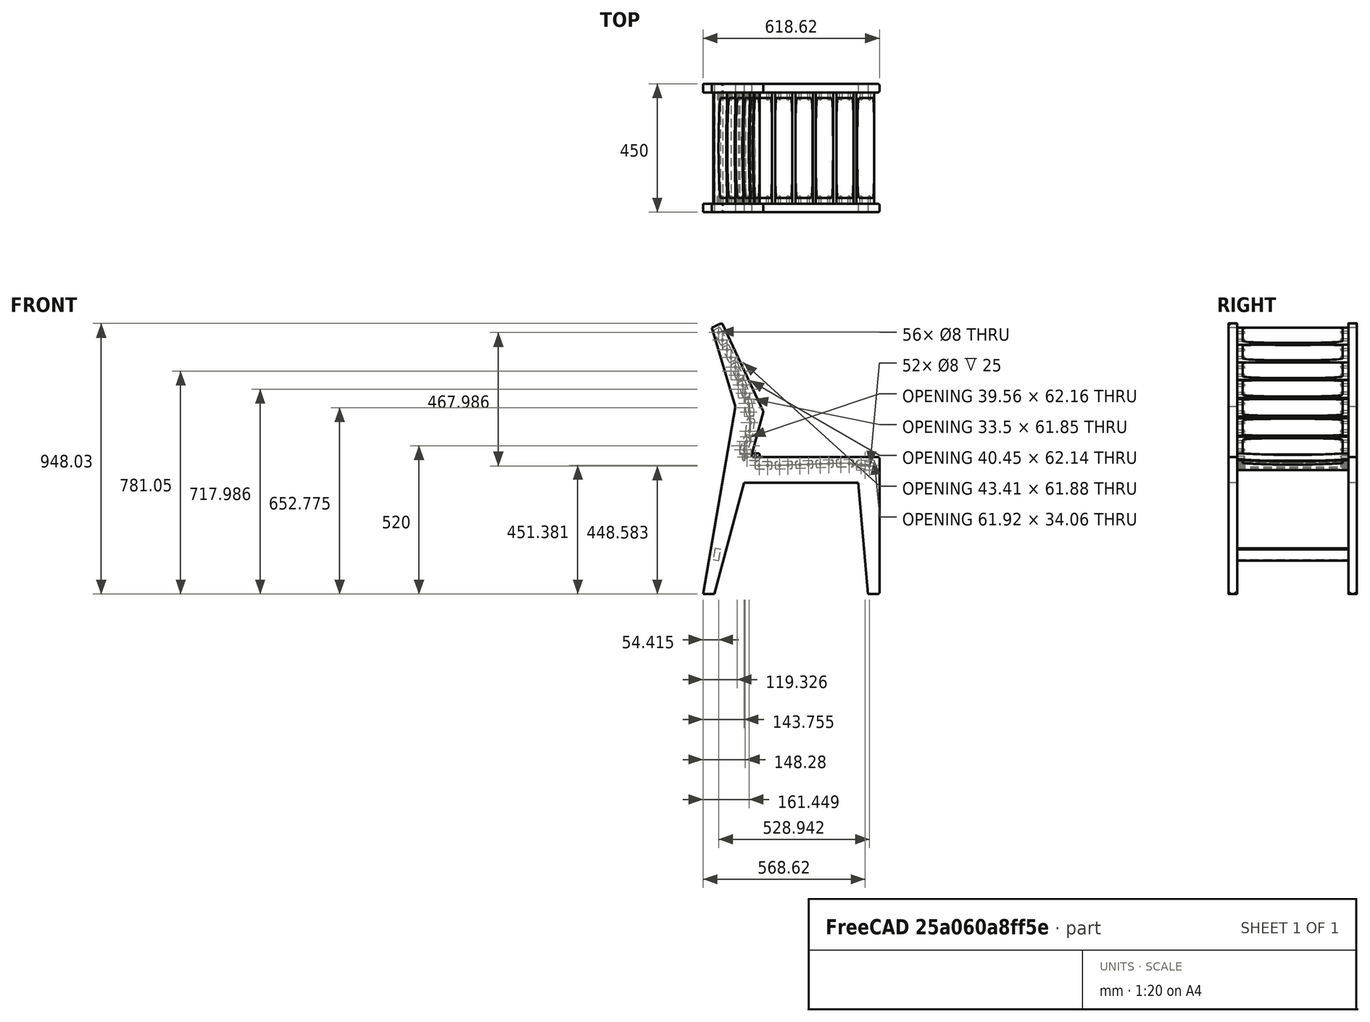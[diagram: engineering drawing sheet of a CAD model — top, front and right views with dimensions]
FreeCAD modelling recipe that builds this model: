
FCSTD DOCUMENT  (FreeCAD 0.21R33771 (Git))
Label: office_v2
License: All rights reserved
LicenseURL: http://en.wikipedia.org/wiki/All_rights_reserved
objects: TechDraw::DrawViewDimension×39, Sketcher::SketchObject×8, PartDesign::Body×4, TechDraw::DrawProjGroupItem×4, PartDesign::Pad×3, Part::FeaturePython×3, TechDraw::DrawSVGTemplate×3, TechDraw::DrawPage×3, PartDesign::Hole×2, PartDesign::SubShapeBinder×2, TechDraw::DrawProjGroup×2, TechDraw::DrawViewBalloon×2, Spreadsheet::Sheet×1, PartDesign::Fillet×1, PartDesign::Pocket×1, TechDraw::DrawViewPart×1, App::Part×1, PartDesign::Boolean×1
note: 92 computed .brp shape members not serialized (recipe doc carries the construction recipe); baked Part::Feature solids carry a one-line shape summary decoded from their .brp

FEATURE [Sketcher::SketchObject] Sketch  label="SideSketch"
  FullyConstrained = true
  Placement = pos=(0,0,0) rot=(1,0,0;1.5708rad)
  expr: Constraints[23] = <<Spreadsheet>>.back_angle
  expr: Constraints[24] = <<Spreadsheet>>.back_leg_angle
  expr: Constraints[29] = <<Spreadsheet>>.seat_length
  expr: Constraints[30] = <<Spreadsheet>>.lumbar_end_height
  expr: Constraints[32] = <<Spreadsheet>>.total_height
  expr: Constraints[5] = <<Spreadsheet>>.seat_height
  sketch-geometry (28):
    g0: LineSegment StartX=0 StartY=0 StartZ=0 EndX=450 EndY=0 EndZ=0
    g1: LineSegment StartX=375.879 StartY=-90 StartZ=0 EndX=-24.1154 EndY=-90 EndZ=0
    g2: LineSegment StartX=450 StartY=0 StartZ=0 EndX=450 EndY=-480 EndZ=0
    g3: LineSegment StartX=450 StartY=-480 StartZ=0 EndX=410 EndY=-480 EndZ=0
    g4: LineSegment StartX=410 StartY=-480 StartZ=0 EndX=368.005 EndY=0 EndZ=0
    g5: LineSegment StartX=-168.616 StartY=-480 StartZ=0 EndX=-128.616 EndY=-480 EndZ=0
    g6: LineSegment StartX=-101.684 StartY=470 StartZ=0 EndX=-137.936 EndY=453.095 EndZ=0
    g7: LineSegment StartX=-137.936 StartY=453.095 StartZ=0 EndX=-55.6825 EndY=176.942 EndZ=0
    g8: LineSegment StartX=-168.616 StartY=-480 StartZ=0 EndX=-55.6825 EndY=176.942 EndZ=0
    g9: LineSegment StartX=-55.6825 StartY=176.942 StartZ=0 EndX=42.8719 EndY=160 EndZ=0
    g10: LineSegment StartX=-128.616 StartY=-480 StartZ=0 EndX=42.8719 EndY=160 EndZ=0
    g11: LineSegment StartX=-101.684 StartY=470 StartZ=0 EndX=42.8719 EndY=160 EndZ=0
    g12: LineSegment StartX=-137.936 StartY=453.095 StartZ=0 EndX=-101.684 EndY=470 EndZ=0
    g13: LineSegment StartX=-101.684 StartY=470 StartZ=0 EndX=42.8719 EndY=160 EndZ=0
    g14: LineSegment StartX=42.8719 StartY=160 StartZ=0 EndX=0 EndY=0 EndZ=0
    g15: LineSegment StartX=0 StartY=0 StartZ=0 EndX=450 EndY=0 EndZ=0
    g16: LineSegment StartX=450 StartY=0 StartZ=0 EndX=450 EndY=-480 EndZ=0
    g17: LineSegment StartX=450 StartY=-480 StartZ=0 EndX=410 EndY=-480 EndZ=0
    g18: LineSegment StartX=410 StartY=-480 StartZ=0 EndX=375.879 EndY=-90 EndZ=0
    g19: LineSegment StartX=375.879 StartY=-90 StartZ=0 EndX=-24.1154 EndY=-90 EndZ=0
    g20: LineSegment StartX=-24.1154 StartY=-90 StartZ=0 EndX=-128.616 EndY=-480 EndZ=0
    g21: LineSegment StartX=-128.616 StartY=-480 StartZ=0 EndX=-168.616 EndY=-480 EndZ=0
    g22: LineSegment StartX=-168.616 StartY=-480 StartZ=0 EndX=-55.6825 EndY=176.942 EndZ=0
    g23: LineSegment StartX=-55.6825 StartY=176.942 StartZ=0 EndX=-137.936 EndY=453.095 EndZ=0
    g24: LineSegment StartX=-125.99 StartY=-320.578 StartZ=0 EndX=-106.279 EndY=-323.967 EndZ=0
    g25: LineSegment StartX=-106.279 StartY=-323.967 StartZ=0 EndX=-113.056 EndY=-363.388 EndZ=0
    g26: LineSegment StartX=-113.056 StartY=-363.388 StartZ=0 EndX=-132.767 EndY=-360 EndZ=0
    g27: LineSegment StartX=-132.767 StartY=-360 StartZ=0 EndX=-125.99 EndY=-320.578 EndZ=0
  constraints (75):
    c: Horizontal(g0)
    c: Horizontal(g1)
    c: Coincident(g2,g3)
    c: Horizontal(g3)
    c: Coincident(g4,g3)
    c: DistanceY(g2,g0) = 480
    c: PointOnObject(g5,g3)
    c: Coincident(g2,g0)
    c: Perpendicular(g2,g0)
    c: DistanceX(g3,g2) = 40
    c: Angle(g1,g4) = 1.65806
    c: Horizontal(g5)
    c: DistanceY(g1,g0) = 90
    c: Coincident(g7,g6)
    c: Coincident(g8,g5)
    c: DistanceX(g5,g5) = 40
    c: Coincident(g7,g8)
    c: Coincident(g9,g7)
    c: Angle(g8,g9) = 1.5708
    c: Coincident(g10,g5)
    c: Coincident(g11,g6)
    c: Coincident(g11,g10)
    c: Coincident(g10,g9)
    c: Angle(g0,g11) = 2.00713
    c: Angle(g10,g1) = 1.8326
    c: PointOnObject(g0,g10)
    c: PointOnObject(g1,g10)
    c: Perpendicular(g11,g6)
    c: Coincident(g0,g-1)
    c: Distance(g0) = 450
    c: Distance(g9,g0) = 160
    c: Distance(g9) = 100
    c: DistanceY(g5,g6) = 950
    c: Equal(g6,g5)
    c: PointOnObject(g4,g0)
    c: PointOnObject(g1,g4)
    c: Coincident(g6,g12)
    c: Coincident(g12,g6)
    c: Coincident(g12,g13)
    c: Coincident(g13,g9)
    c: Coincident(g13,g14)
    c: Coincident(g14,g0)
    c: Coincident(g14,g15)
    c: Coincident(g15,g0)
    c: Coincident(g15,g16)
    c: Coincident(g16,g2)
    c: Coincident(g16,g17)
    c: Coincident(g17,g3)
    c: Coincident(g17,g18)
    c: Coincident(g18,g1)
    c: Coincident(g18,g19)
    c: Coincident(g19,g1)
    c: Coincident(g19,g20)
    c: Coincident(g20,g5)
    c: Coincident(g20,g21)
    c: Coincident(g21,g5)
    c: Coincident(g21,g22)
    c: Coincident(g22,g7)
    c: Coincident(g22,g23)
    c: Coincident(g23,g12)
    c: Coincident(g24,g25)
    c: Coincident(g25,g26)
    c: Coincident(g26,g27)
    c: Coincident(g27,g24)
    c: Perpendicular(g25,g24)
    c: Perpendicular(g26,g25)
    c: Perpendicular(g26,g27)
    c: Parallel(g27,g22)
    c: Distance(g24,g22) = 15
    c: Distance(g25) = 40
    c: DistanceY(g20,g26) = 120
    c: Distance(g26) = 20
    c: Angle(g12,g13) = 1.5708
    c: Angle(g13,g9) = 0.964221
    c: Angle(g9,g23) = 2.03053
FEATURE [Spreadsheet::Sheet] Spreadsheet
  cells = A1='seat length; B1(seat_length)=450; A2='seat height; B2(seat_height)=480; A3='back angle; B3(back_angle)=115; A4='chair width; B4(chair_width)=450; A5='slats thickness; B5(slat_thickness)=25; A6='back slats height; B6(back_slat_width)=60; A7='seat slats width; B7(seat_slat_width)=80; A8='seat slats thickness; B8(seat_slat_thickness)=20; A9='total height; B9(total_height)=950; A10='lumbar support end height; B10(lumbar_end_height)=160; A11='back slat gap; B11(back_slat_gap)=15; A12='back slat thickness; B12(back_slat_thickness)=20; A13='seat slat gap; B13(seat_slat_gap)=10; A14='back leg angle to surface; B14(back_leg_angle)=105; A15='draft back; B15(draft_back)=5; A16='side thickness; B16(side_thickness)=30; A17='slat_width; B17(slat_width)=60; A18='slat_chamfer_radius; B18(slat_chamfer_radius)=5
FEATURE [PartDesign::Pad] Pad
  Direction = (0,-1,2e-16)
  Length = 30
  Length2 = 10
  Placement = pos=(0,0,0) rot=(1,0,0;1.5708rad)
  Profile = -> Sketch
  ReferenceAxis = -> Sketch [N_Axis]
  Type = 0
  expr: Length = <<Spreadsheet>>.side_thickness
FEATURE [PartDesign::Fillet] Fillet
  Base = -> Pad [Face2,Face3,Face4,Face5]
  BaseFeature = -> Pad
  Placement = pos=(0,0,0) rot=(1,0,0;1.5708rad)
  Radius = 6
  SupportTransform = false
  UseAllEdges = false
FEATURE [PartDesign::Body] Body  label="LeftSide"
  Group = -> [Sketch,Pad,Fillet]
  Origin = -> Origin
  Tip = -> Fillet
FEATURE [Sketcher::SketchObject] Sketch001  label="curves"
  ExternalGeometry = -> [Sketch]
  FullyConstrained = false
  MapMode = 5
  Placement = pos=(0,-1.72e-14,0) rot=(-1,0,0;1.5708rad)
  Support = -> [Pad]
  sketch-geometry (23):
    g0: LineSegment StartX=375.879 StartY=90 StartZ=0 EndX=368.005 EndY=0 EndZ=0
    g1: LineSegment StartX=0 StartY=0 StartZ=0 EndX=-24.1154 EndY=90 EndZ=0
    g2: LineSegment StartX=42.8719 StartY=-160 StartZ=0 EndX=-55.6825 EndY=-176.942 EndZ=0
    g3: Circle CenterX=-107.436 CenterY=-423.182 CenterZ=0 NormalX=0 NormalY=0 NormalZ=1 AngleXU=0 Radius=1
    g4: Circle CenterX=4.19663 CenterY=-116.283 CenterZ=0 NormalX=0 NormalY=0 NormalZ=1 AngleXU=0 Radius=1
    g5: Circle CenterX=-20.3403 CenterY=-40 CenterZ=0 NormalX=0 NormalY=0 NormalZ=1 AngleXU=0 Radius=1
    g6: BSplineCurve PolesCount=6 KnotsCount=4 Degree=3 IsPeriodic=0
    g7: GeomPoint X=-107.436 Y=-423.182 Z=0
    g8: GeomPoint X=-6.41239 Y=-168.472 Z=0
    g9: GeomPoint X=-20.3403 Y=-40 Z=0
    g10: Circle CenterX=-67.1086 CenterY=-343.425 CenterZ=0 NormalX=0 NormalY=0 NormalZ=1 AngleXU=0 Radius=0.962105
    g11: Circle CenterX=-16.1135 CenterY=-229.617 CenterZ=0 NormalX=0 NormalY=0 NormalZ=1 AngleXU=0 Radius=0.629843
    g12: Circle CenterX=-5.01988 CenterY=-156.601 CenterZ=0 NormalX=0 NormalY=0 NormalZ=1 AngleXU=0 Radius=1
    g13: GeomPoint X=-31.7882 Y=-257.283 Z=0
    g14: Circle CenterX=400 CenterY=28.6187 CenterZ=0 NormalX=0 NormalY=0 NormalZ=1 AngleXU=0 Radius=1
    g15: Circle CenterX=43.0206 CenterY=29.1813 CenterZ=0 NormalX=0 NormalY=0 NormalZ=1 AngleXU=0 Radius=1
    g16: BSplineCurve PolesCount=5 KnotsCount=3 Degree=3 IsPeriodic=0
    g17: GeomPoint X=400 Y=28.6187 Z=0
    g18: GeomPoint X=43.0206 Y=29.1813 Z=0
    g19: Circle CenterX=358.23 CenterY=20.6863 CenterZ=0 NormalX=0 NormalY=0 NormalZ=1 AngleXU=0 Radius=1
    g20: Circle CenterX=277.297 CenterY=21.6556 CenterZ=0 NormalX=0 NormalY=0 NormalZ=1 AngleXU=0 Radius=1
    g21: Circle CenterX=111.923 CenterY=30.2855 CenterZ=0 NormalX=0 NormalY=0 NormalZ=1 AngleXU=0 Radius=1
    g22: GeomPoint X=274.038 Y=22.8992 Z=0
  constraints (40):
    c: Coincident(g0,g-6)
    c: Parallel(g0,g-5)
    c: Coincident(g1,g-14)
    c: Coincident(g1,g-7)
    c: PointOnObject(g0,g-14)
    c: Coincident(g2,g-13)
    c: Coincident(g2,g-10)
    c: Weight(g3) = 1
    c: Equal(g3,g4)
    c: Equal(g3,g5)
    c: InternalAlignment(g3,g6)
    c: InternalAlignment(g4,g6)
    c: InternalAlignment(g5,g6)
    c: InternalAlignment(g7,g6)
    c: InternalAlignment(g8,g6)
    c: InternalAlignment(g9,g6)
    c: Distance(g6,g-11) = 40
    c: DistanceY(g-1,g6) = -40
    c: InternalAlignment(g10,g6)
    c: InternalAlignment(g11,g6)
    c: InternalAlignment(g12,g6)
    c: Equal(g12,g3)
    c: InternalAlignment(g13,g6)
    c: Distance(g6,g-12) = 25
    c: Distance(g6,g-13) = 30
    c: PointOnObject(g8,g2)
    c: Weight(g14) = 1
    c: Equal(g14,g15)
    c: InternalAlignment(g14,g16)
    c: InternalAlignment(g15,g16)
    c: InternalAlignment(g17,g16)
    c: InternalAlignment(g18,g16)
    c: Distance(g16,g-3) = 50
    c: InternalAlignment(g19,g16)
    c: Equal(g19,g14)
    c: InternalAlignment(g20,g16)
    c: Equal(g20,g14)
    c: InternalAlignment(g21,g16)
    c: Equal(g21,g14)
    c: InternalAlignment(g22,g16)
FEATURE [Sketcher::SketchObject] Sketch002  label="slat_profile"
  FullyConstrained = true
  MapMode = 5
  Placement = pos=(0,0,0) rot=(1,0,0;1.5708rad)
  Support = -> [XZ_Plane001]
  expr: Constraints[15] = <<Spreadsheet>>.slat_width
  expr: Constraints[16] = <<Spreadsheet>>.slat_thickness
  expr: Constraints[17] = <<Spreadsheet>>.slat_chamfer_radius
  sketch-geometry (9):
    g0: ArcOfCircle CenterX=25 CenterY=-7.5 CenterZ=0 NormalX=0 NormalY=0 NormalZ=1 AngleXU=0 Radius=5 StartAngle=4.71239 EndAngle=6.28319
    g1: LineSegment StartX=25 StartY=-12.5 StartZ=0 EndX=-25 EndY=-12.5 EndZ=0
    g2: ArcOfCircle CenterX=-25 CenterY=-7.5 CenterZ=0 NormalX=0 NormalY=0 NormalZ=1 AngleXU=0 Radius=5 StartAngle=3.14159 EndAngle=4.71239
    g3: LineSegment StartX=-30 StartY=-7.5 StartZ=0 EndX=-30 EndY=7.5 EndZ=0
    g4: ArcOfCircle CenterX=-25 CenterY=7.5 CenterZ=0 NormalX=0 NormalY=0 NormalZ=1 AngleXU=0 Radius=5 StartAngle=1.5708 EndAngle=3.14159
    g5: LineSegment StartX=-25 StartY=12.5 StartZ=0 EndX=25 EndY=12.5 EndZ=0
    g6: ArcOfCircle CenterX=25 CenterY=7.5 CenterZ=0 NormalX=0 NormalY=0 NormalZ=1 AngleXU=0 Radius=5 StartAngle=1e-16 EndAngle=1.5708
    g7: LineSegment StartX=30 StartY=7.5 StartZ=0 EndX=30 EndY=-7.5 EndZ=0
    g8: GeomPoint X=-30 Y=12.5 Z=0
  constraints (20):
    c: Tangent(g0,g1) = 1.5708
    c: Tangent(g1,g2) = 1.5708
    c: Tangent(g2,g3) = 1.5708
    c: Tangent(g3,g4) = 1.5708
    c: Tangent(g4,g5) = 1.5708
    c: Tangent(g5,g6) = 1.5708
    c: Tangent(g6,g7) = 1.5708
    c: Tangent(g7,g0) = 1.5708
    c: Equal(g0,g2)
    c: Equal(g2,g4)
    c: Equal(g4,g6)
    c: PointOnObject(g8,g3)
    c: PointOnObject(g8,g5)
    c: Parallel(g5,g1)
    c: Perpendicular(g1,g7)
    c: Distance(g6,g3) = 60
    c: Distance(g1,g4) = 25
    c: Distance(g2,g2) = 5
    c: Symmetric(g3,g6,g-2)
    c: Symmetric(g5,g0,g-1)
FEATURE [PartDesign::Pad] Pad001
  Direction = (0,-1,2e-16)
  Length = 390
  Length2 = 10
  Placement = pos=(0,0,0) rot=(1,0,0;1.5708rad)
  Profile = -> Sketch002
  ReferenceAxis = -> Sketch002 [N_Axis]
  Reversed = true
  Type = 0
  expr: Length = <<Spreadsheet>>.chair_width - <<Spreadsheet>>.side_thickness * 2
FEATURE [Sketcher::SketchObject] Sketch003
  ExternalGeometry = -> [Pad001]
  FullyConstrained = true
  MapMode = 5
  Placement = pos=(0,0,0) rot=(1,0,0;1.5708rad)
  Support = -> [Pad001]
  expr: Constraints[0] = <<Spreadsheet>>.slat_thickness / 2
  sketch-geometry (2):
    g0: Circle CenterX=15 CenterY=-7.1e-15 CenterZ=0 NormalX=0 NormalY=0 NormalZ=1 AngleXU=0 Radius=4
    g1: Circle CenterX=-15 CenterY=0 CenterZ=0 NormalX=0 NormalY=0 NormalZ=1 AngleXU=0 Radius=4
  constraints (7):
    c: Distance(g0,g-3) = 12.5
    c: Distance(g0,g-4) = 15
    c: Diameter(g0) = 8
    c: Diameter(g1) = 8
    c: PointOnObject(g1,g-1)
    c: Distance(g1,g-5) = 15
    c: Distance(g1,g0) = 30
FEATURE [PartDesign::Hole] Hole
  BaseFeature = -> Pad001
  CustomThreadClearance = 0
  Depth = 25
  DepthType = 0
  Diameter = 8
  DrillForDepth = false
  DrillPoint = 1
  DrillPointAngle = 118
  HoleCutCountersinkAngle = 90
  HoleCutCustomValues = false
  HoleCutDepth = 0
  HoleCutDiameter = 6.1
  HoleCutType = 0
  ModelThread = false
  Placement = pos=(0,0,0) rot=(1,0,0;1.5708rad)
  Profile = -> Sketch003
  Tapered = false
  TaperedAngle = 90
  ThreadClass = 0
  ThreadDepth = 25
  ThreadDepthType = 0
  ThreadDirection = 0
  ThreadFit = 0
  ThreadSize = 0
  ThreadType = 0
  Threaded = false
  UseCustomThreadClearance = false
FEATURE [PartDesign::SubShapeBinder] Binder
  BindCopyOnChange = 0
  BindMode = 0
  ClaimChildren = false
  Context = -> Body001 [Binder.]
  Fuse = false
  MakeFace = true
  OffsetFill = false
  OffsetIntersection = false
  OffsetJoinType = 0
  OffsetOpenResult = false
  PartialLoad = false
  Relative = true
  Support = -> [Body]
  _Version = 2
FEATURE [Sketcher::SketchObject] Sketch004
  ExternalGeometry = -> [Hole]
  FullyConstrained = true
  MapMode = 5
  Placement = pos=(0,390,0) rot=(-1,0,0;1.5708rad)
  Support = -> [Hole]
  sketch-geometry (2):
    g0: Circle CenterX=-15 CenterY=0 CenterZ=0 NormalX=0 NormalY=0 NormalZ=1 AngleXU=0 Radius=4
    g1: Circle CenterX=15 CenterY=0 CenterZ=0 NormalX=0 NormalY=0 NormalZ=1 AngleXU=0 Radius=4
  constraints (6):
    c: PointOnObject(g0,g-1)
    c: PointOnObject(g1,g-1)
    c: Diameter(g0) = 8
    c: Diameter(g1) = 8
    c: Distance(g1,g-4) = 15
    c: Distance(g0,g-6) = 15
FEATURE [PartDesign::Hole] Hole001
  BaseFeature = -> Hole
  CustomThreadClearance = 0
  Depth = 25
  DepthType = 0
  Diameter = 8
  DrillForDepth = false
  DrillPoint = 1
  DrillPointAngle = 118
  HoleCutCountersinkAngle = 90
  HoleCutCustomValues = false
  HoleCutDepth = 0
  HoleCutDiameter = 6.1
  HoleCutType = 0
  ModelThread = false
  Placement = pos=(0,0,0) rot=(1,0,0;1.5708rad)
  Profile = -> Sketch004
  Tapered = false
  TaperedAngle = 90
  ThreadClass = 0
  ThreadDepth = 25
  ThreadDepthType = 0
  ThreadDirection = 0
  ThreadFit = 0
  ThreadSize = 0
  ThreadType = 0
  Threaded = false
  UseCustomThreadClearance = false
FEATURE [Part::FeaturePython] Clone  label="RightSide"  # Draft clone (typed FeaturePython)
  AttacherType = Attacher::AttachEngine3D
  Fuse = false
  Objects = -> [Body]
  Placement = pos=(0,420,0) rot=(0,0,1;0rad)
  Scale = (1,1,1)
  expr: .Placement.Base.y = <<Spreadsheet>>.chair_width - <<Spreadsheet>>.side_thickness
FEATURE [Sketcher::SketchObject] Sketch005
  ExternalGeometry = -> [Hole001]
  FullyConstrained = true
  MapMode = 5
  Placement = pos=(30,0,0) rot=(0.707107,0,0.707107;3.14159rad)
  Support = -> [Hole001]
  sketch-geometry (4):
    g0: GeomPoint X=12.5 Y=-20 Z=0
    g1: GeomPoint X=12.5 Y=-370 Z=0
    g2: ArcOfCircle CenterX=3072.5 CenterY=-195 CenterZ=0 NormalX=0 NormalY=0 NormalZ=1 AngleXU=0 Radius=3065 StartAngle=3.08447 EndAngle=3.19872
    g3: LineSegment StartX=12.5 StartY=-20 StartZ=0 EndX=12.5 EndY=-370 EndZ=0
  constraints (9):
    c: PointOnObject(g0,g-3)
    c: PointOnObject(g1,g-3)
    c: Distance(g0,g-3) = 20
    c: Distance(g1,g-3) = 20
    c: Coincident(g2,g0)
    c: Coincident(g2,g1)
    c: Tangent(g2,g-4)
    c: Coincident(g3,g2)
    c: Coincident(g3,g2)
FEATURE [PartDesign::Pocket] Pocket
  BaseFeature = -> Hole001
  Direction = (-1,0,2e-16)
  Length = 64
  Length2 = 5
  Placement = pos=(0,0,0) rot=(1,0,0;1.5708rad)
  Profile = -> Sketch005
  ReferenceAxis = -> Sketch005 [N_Axis]
  Type = 4
FEATURE [PartDesign::Body] Body001  label="Slat"
  Group = -> [Sketch002,Pad001,Sketch003,Hole,Binder,Sketch001,Sketch004,Hole001,Sketch005,Pocket]
  Origin = -> Origin001
  Tip = -> Pocket
FEATURE [PartDesign::SubShapeBinder] Binder001
  BindCopyOnChange = 0
  BindMode = 0
  ClaimChildren = false
  Context = -> Body002 [Binder001.]
  Fuse = false
  MakeFace = true
  OffsetFill = false
  OffsetIntersection = false
  OffsetJoinType = 0
  OffsetOpenResult = false
  PartialLoad = false
  Relative = true
  Support = -> [Body[Fillet.Face2]]
  _Version = 2
FEATURE [Sketcher::SketchObject] Sketch006
  ExternalGeometry = -> [Binder001]
  FullyConstrained = true
  MapMode = 5
  Placement = pos=(0,0,0) rot=(1,0,0;1.5708rad)
  Support = -> [XZ_Plane002]
  sketch-geometry (4):
    g0: LineSegment StartX=-106.279 StartY=-323.967 StartZ=0 EndX=-125.99 EndY=-320.578 EndZ=0
    g1: LineSegment StartX=-125.99 StartY=-320.578 StartZ=0 EndX=-132.767 EndY=-360 EndZ=0
    g2: LineSegment StartX=-132.767 StartY=-360 StartZ=0 EndX=-113.056 EndY=-363.388 EndZ=0
    g3: LineSegment StartX=-113.056 StartY=-363.388 StartZ=0 EndX=-106.279 EndY=-323.967 EndZ=0
  constraints (12):
    c: Coincident(g0,g1)
    c: Coincident(g1,g2)
    c: Coincident(g2,g3)
    c: Coincident(g3,g0)
    c: Distance(g1) = 40
    c: Distance(g0) = 20
    c: Parallel(g0,g2)
    c: Parallel(g3,g1)
    c: Parallel(g1,g-3)
    c: Perpendicular(g2,g3)
    c: DistanceY(g-5,g1) = 120
    c: Distance(g1,g-3) = 15
FEATURE [PartDesign::Pad] Pad002
  Direction = (0,-1,-2e-16)
  Length = 390
  Length2 = 10
  Placement = pos=(0,0,0) rot=(1,0,0;1.5708rad)
  Profile = -> Sketch006
  ReferenceAxis = -> Sketch006 [N_Axis]
  Reversed = true
  Type = 0
  expr: Length = <<Spreadsheet>>.chair_width - 2 * <<Spreadsheet>>.side_thickness
FEATURE [PartDesign::Body] Body002  label="Stretcher"
  Group = -> [Binder001,Sketch006,Pad002]
  Origin = -> Origin002
  Tip = -> Pad002
FEATURE [Part::FeaturePython] PathArray001  label="SeatSlats"  # WARN: FeaturePython — macro-defined, semantics opaque (R4)
  Align = true
  AlignMode = 2
  Base = -> Pocket
  Count = 6
  EndOffset = 0
  ExtraTranslation = (0,0,0)
  ForceVertical = true
  PathObject = -> Sketch001
  PathSubelements = -> [Sketch001]
  Placement = pos=(0,390,0) rot=(0,0,1;0rad)
  StartOffset = 0
  TangentVector = (1,0,0)
  VerticalVector = (0,0,1)
  expr: .Placement.Base.y = <<Spreadsheet>>.chair_width - 2 * <<Spreadsheet>>.side_thickness
FEATURE [Part::FeaturePython] PathArray  label="BackSlats"  # WARN: FeaturePython — macro-defined, semantics opaque (R4)
  Align = true
  AlignMode = 0
  Base = -> Pocket
  Count = 7
  EndOffset = 0
  ExtraTranslation = (0,0,0)
  ForceVertical = false
  PathObject = -> Sketch001
  PathSubelements = -> [Sketch001]
  StartOffset = 0
  TangentVector = (1,0,0)
  VerticalVector = (0,0,1)
FEATURE [TechDraw::DrawSVGTemplate] Template
  Height = 594
  Orientation = 1
  Template = <path>
  Width = 841
FEATURE [TechDraw::DrawViewPart] View002
  CoarseView = false
  Direction = (0,1,0)
  Focus = 100
  HardHidden = false
  IsoCount = 0
  IsoHidden = false
  IsoVisible = false
  LockPosition = false
  Perspective = false
  Rotation = 280
  ScaleType = 0
  ScrubCount = 0
  SeamHidden = false
  SeamVisible = false
  SmoothHidden = false
  SmoothVisible = true
  Source = -> [Pad,PathArray,PathArray001]
  X = 153.16
  XDirection = (-1,0,0)
  Y = 240.179
FEATURE [TechDraw::DrawViewDimension] Dimension
  AngleOverride = false
  Arbitrary = false
  ArbitraryTolerances = false
  EqualTolerance = true
  ExtensionAngle = 0
  FormatSpec = ⌀%.2w
  FormatSpecOverTolerance = %+.2w
  FormatSpecUnderTolerance = %+.2w
  Inverted = false
  LineAngle = 0
  LockPosition = false
  MeasureType = 1
  OverTolerance = 0
  References2D = -> [View002]
  Rotation = 0
  ScaleType = 0
  TheoreticalExact = false
  Type = 5
  UnderTolerance = 0
  X = -67.7505
  Y = 256.25
FEATURE [TechDraw::DrawSVGTemplate] Template001
  Height = 215.9
  Orientation = 1
  Template = <path>
  Width = 279.4
FEATURE [TechDraw::DrawProjGroupItem] ProjItem  label="Front"
  CoarseView = false
  Direction = (1,0,0)
  Focus = 100
  HardHidden = false
  IsoCount = 0
  IsoHidden = false
  IsoVisible = false
  LockPosition = true
  Perspective = false
  Rotation = 0
  RotationVector = (0,1,0)
  Scale = 0.5
  ScaleType = 2
  ScrubCount = 0
  SeamHidden = false
  SeamVisible = false
  SmoothHidden = false
  SmoothVisible = true
  Source = -> [Pocket]
  Type = 0
  X = 0
  XDirection = (0,1,2e-16)
  Y = 0
FEATURE [TechDraw::DrawProjGroupItem] ProjItem001  label="Top"
  CoarseView = false
  Direction = (0,-2e-16,1)
  Focus = 100
  HardHidden = false
  IsoCount = 0
  IsoHidden = false
  IsoVisible = false
  LockPosition = false
  Perspective = false
  Rotation = 0
  RotationVector = (1,0,0)
  ScaleType = 2
  ScrubCount = 0
  SeamHidden = false
  SeamVisible = false
  SmoothHidden = false
  SmoothVisible = true
  Source = -> [Pocket]
  Type = 4
  X = 0
  XDirection = (0,1,2e-16)
  Y = -36.25
FEATURE [TechDraw::DrawProjGroupItem] ProjItem002  label="Left"
  CoarseView = false
  Direction = (1e-16,-1,-2e-16)
  Focus = 100
  HardHidden = false
  IsoCount = 0
  IsoHidden = false
  IsoVisible = false
  LockPosition = false
  Perspective = false
  Rotation = 0
  RotationVector = (1,0,0)
  ScaleType = 2
  ScrubCount = 0
  SeamHidden = false
  SeamVisible = false
  SmoothHidden = false
  SmoothVisible = true
  Source = -> [Pocket]
  Type = 1
  X = 127.5
  XDirection = (1,1e-16,0)
  Y = 0
FEATURE [TechDraw::DrawProjGroup] ProjGroup
  Anchor = -> ProjItem
  AutoDistribute = true
  LockPosition = false
  ProjectionType = 0
  Rotation = 0
  Scale = 0.5
  ScaleType = 2
  Source = -> [Pocket]
  Views = -> [ProjItem,ProjItem001,ProjItem002]
  X = 115.867
  Y = 123.966
  spacingX = 15
  spacingY = 15
FEATURE [TechDraw::DrawViewDimension] Dimension001
  AngleOverride = false
  Arbitrary = false
  ArbitraryTolerances = false
  EqualTolerance = true
  ExtensionAngle = 0
  FormatSpec = %.2w
  FormatSpecOverTolerance = %+.2w
  FormatSpecUnderTolerance = %+.2w
  Inverted = false
  LineAngle = 0
  LockPosition = false
  MeasureType = 1
  OverTolerance = 0
  References2D = -> [ProjItem]
  Rotation = 0
  ScaleType = 0
  TheoreticalExact = false
  Type = 1
  UnderTolerance = 0
  X = -92.9545
  Y = 15.6989
FEATURE [TechDraw::DrawViewDimension] Dimension003
  AngleOverride = false
  Arbitrary = false
  ArbitraryTolerances = false
  EqualTolerance = true
  ExtensionAngle = 0
  FormatSpec = ⌀%.2w
  FormatSpecOverTolerance = %+.2w
  FormatSpecUnderTolerance = %+.2w
  Inverted = false
  LineAngle = 0
  LockPosition = false
  MeasureType = 1
  OverTolerance = 0
  References2D = -> [ProjItem002]
  Rotation = 0
  ScaleType = 0
  TheoreticalExact = false
  Type = 5
  UnderTolerance = 0
  X = -4.33544
  Y = 3.01756
FEATURE [TechDraw::DrawViewDimension] Dimension004
  AngleOverride = false
  Arbitrary = false
  ArbitraryTolerances = false
  EqualTolerance = true
  ExtensionAngle = 0
  FormatSpec = %.2w
  FormatSpecOverTolerance = %+.2w
  FormatSpecUnderTolerance = %+.2w
  Inverted = false
  LineAngle = 0
  LockPosition = false
  MeasureType = 1
  OverTolerance = 0
  References2D = -> [ProjItem002]
  Rotation = 0
  ScaleType = 0
  TheoreticalExact = false
  Type = 1
  UnderTolerance = 0
  X = -0.367799
  Y = -20.9158
FEATURE [TechDraw::DrawViewDimension] Dimension005
  AngleOverride = false
  Arbitrary = false
  ArbitraryTolerances = false
  EqualTolerance = true
  ExtensionAngle = 0
  FormatSpec = %.2w
  FormatSpecOverTolerance = %+.2w
  FormatSpecUnderTolerance = %+.2w
  Inverted = false
  LineAngle = 0
  LockPosition = false
  MeasureType = 1
  OverTolerance = 0
  References2D = -> [ProjItem002]
  Rotation = 0
  ScaleType = 0
  TheoreticalExact = false
  Type = 2
  UnderTolerance = 0
  X = 22.7064
  Y = 2.0517
FEATURE [TechDraw::DrawViewDimension] Dimension006
  AngleOverride = false
  Arbitrary = false
  ArbitraryTolerances = false
  EqualTolerance = true
  ExtensionAngle = 0
  FormatSpec = %.2w
  FormatSpecOverTolerance = %+.2w
  FormatSpecUnderTolerance = %+.2w
  Inverted = false
  LineAngle = 0
  LockPosition = false
  MeasureType = 1
  OverTolerance = 0
  References2D = -> [ProjItem]
  Rotation = 0
  ScaleType = 0
  TheoreticalExact = false
  Type = 1
  UnderTolerance = 0
  X = 92.5
  Y = 15.0773
FEATURE [TechDraw::DrawViewDimension] Dimension007
  AngleOverride = false
  Arbitrary = false
  ArbitraryTolerances = false
  EqualTolerance = true
  ExtensionAngle = 0
  FormatSpec = %.2w
  FormatSpecOverTolerance = %+.2w
  FormatSpecUnderTolerance = %+.2w
  Inverted = false
  LineAngle = 0
  LockPosition = false
  MeasureType = 1
  OverTolerance = 0
  References2D = -> [ProjItem]
  Rotation = 0
  ScaleType = 0
  TheoreticalExact = false
  Type = 1
  UnderTolerance = 0
  X = 4.16648
  Y = -64.6611
FEATURE [TechDraw::DrawViewDimension] Dimension008
  AngleOverride = false
  Arbitrary = false
  ArbitraryTolerances = false
  EqualTolerance = true
  ExtensionAngle = 0
  FormatSpec = %.2w
  FormatSpecOverTolerance = %+.2w
  FormatSpecUnderTolerance = %+.2w
  Inverted = false
  LineAngle = 0
  LockPosition = false
  MeasureType = 1
  OverTolerance = 0
  References2D = -> [ProjItem]
  Rotation = 0
  ScaleType = 0
  TheoreticalExact = false
  Type = 2
  UnderTolerance = 0
  X = -101.291
  Y = 6.69954
FEATURE [Sketcher::SketchObject] Sketch007  label="SideSketchCopy"
  FullyConstrained = true
  Placement = pos=(0,0,0) rot=(1,0,0;1.5708rad)
  expr: Constraints[23] = <<Spreadsheet>>.back_angle
  expr: Constraints[24] = <<Spreadsheet>>.back_leg_angle
  expr: Constraints[29] = <<Spreadsheet>>.seat_length
  expr: Constraints[30] = <<Spreadsheet>>.lumbar_end_height
  expr: Constraints[32] = <<Spreadsheet>>.total_height
  expr: Constraints[5] = <<Spreadsheet>>.seat_height
  sketch-geometry (38):
    g0: LineSegment StartX=0 StartY=0 StartZ=0 EndX=450 EndY=0 EndZ=0
    g1: LineSegment StartX=375.879 StartY=-90 StartZ=0 EndX=-24.1154 EndY=-90 EndZ=0
    g2: LineSegment StartX=450 StartY=0 StartZ=0 EndX=450 EndY=-480 EndZ=0
    g3: LineSegment StartX=450 StartY=-480 StartZ=0 EndX=410 EndY=-480 EndZ=0
    g4: LineSegment StartX=410 StartY=-480 StartZ=0 EndX=368.005 EndY=0 EndZ=0
    g5: LineSegment StartX=-168.616 StartY=-480 StartZ=0 EndX=-128.616 EndY=-480 EndZ=0
    g6: LineSegment StartX=-101.684 StartY=470 StartZ=0 EndX=-137.936 EndY=453.095 EndZ=0
    g7: LineSegment StartX=-137.936 StartY=453.095 StartZ=0 EndX=-55.6825 EndY=176.942 EndZ=0
    g8: LineSegment StartX=-168.616 StartY=-480 StartZ=0 EndX=-55.6825 EndY=176.942 EndZ=0
    g9: LineSegment StartX=-55.6825 StartY=176.942 StartZ=0 EndX=42.8719 EndY=160 EndZ=0
    g10: LineSegment StartX=-128.616 StartY=-480 StartZ=0 EndX=42.8719 EndY=160 EndZ=0
    g11: LineSegment StartX=-101.684 StartY=470 StartZ=0 EndX=42.8719 EndY=160 EndZ=0
    g12: LineSegment StartX=-137.936 StartY=453.095 StartZ=0 EndX=-101.684 EndY=470 EndZ=0
    g13: LineSegment StartX=-101.684 StartY=470 StartZ=0 EndX=42.8719 EndY=160 EndZ=0
    g14: LineSegment StartX=42.8719 StartY=160 StartZ=0 EndX=0 EndY=0 EndZ=0
    g15: LineSegment StartX=0 StartY=0 StartZ=0 EndX=450 EndY=0 EndZ=0
    g16: LineSegment StartX=450 StartY=0 StartZ=0 EndX=450 EndY=-480 EndZ=0
    g17: LineSegment StartX=450 StartY=-480 StartZ=0 EndX=410 EndY=-480 EndZ=0
    g18: LineSegment StartX=410 StartY=-480 StartZ=0 EndX=375.879 EndY=-90 EndZ=0
    g19: LineSegment StartX=375.879 StartY=-90 StartZ=0 EndX=-24.1154 EndY=-90 EndZ=0
    g20: LineSegment StartX=-24.1154 StartY=-90 StartZ=0 EndX=-128.616 EndY=-480 EndZ=0
    g21: LineSegment StartX=-128.616 StartY=-480 StartZ=0 EndX=-168.616 EndY=-480 EndZ=0
    g22: LineSegment StartX=-168.616 StartY=-480 StartZ=0 EndX=-55.6825 EndY=176.942 EndZ=0
    g23: LineSegment StartX=-55.6825 StartY=176.942 StartZ=0 EndX=-137.936 EndY=453.095 EndZ=0
    g24: LineSegment StartX=-24.1154 StartY=-90 StartZ=0 EndX=3.6e-15 EndY=0 EndZ=0
    g25: LineSegment StartX=368.005 StartY=0 StartZ=0 EndX=375.879 EndY=-90 EndZ=0
    g26: LineSegment StartX=-55.6825 StartY=176.942 StartZ=0 EndX=42.8719 EndY=160 EndZ=0
    g27: LineSegment StartX=-168.616 StartY=-480 StartZ=0 EndX=-130.377 EndY=-486.573 EndZ=0
    g28: LineSegment StartX=-130.377 StartY=-486.573 StartZ=0 EndX=-128.616 EndY=-480 EndZ=0
    g29: LineSegment StartX=61.7657 StartY=230.513 StartZ=0 EndX=42.8719 EndY=160 EndZ=0
    g30: LineSegment StartX=450 StartY=0 StartZ=0 EndX=368.005 EndY=0 EndZ=0
    g31: LineSegment StartX=42.8719 StartY=160 StartZ=0 EndX=0 EndY=0 EndZ=0
    g32: LineSegment StartX=-124.296 StartY=-310.723 StartZ=0 EndX=-104.585 EndY=-314.111 EndZ=0
    g33: LineSegment StartX=-104.585 StartY=-314.111 StartZ=0 EndX=-113.056 EndY=-363.388 EndZ=0
    g34: LineSegment StartX=-113.056 StartY=-363.388 StartZ=0 EndX=-132.767 EndY=-360 EndZ=0
    g35: LineSegment StartX=-132.767 StartY=-360 StartZ=0 EndX=-124.296 EndY=-310.723 EndZ=0
    g36: LineSegment StartX=18.7802 StartY=211.665 StartZ=0 EndX=-55.6825 EndY=176.942 EndZ=0
    g37: LineSegment StartX=61.7657 StartY=230.513 StartZ=0 EndX=2.59858 EndY=246.366 EndZ=0
  constraints (96):
    c: Horizontal(g0)
    c: Horizontal(g1)
    c: Coincident(g2,g3)
    c: Horizontal(g3)
    c: Coincident(g4,g3)
    c: DistanceY(g2,g0) = 480
    c: PointOnObject(g5,g3)
    c: Coincident(g2,g0)
    c: Perpendicular(g2,g0)
    c: DistanceX(g3,g2) = 40
    c: Angle(g1,g4) = 1.65806
    c: Horizontal(g5)
    c: DistanceY(g1,g0) = 90
    c: Coincident(g7,g6)
    c: Coincident(g8,g5)
    c: DistanceX(g5,g5) = 40
    c: Coincident(g7,g8)
    c: Coincident(g9,g7)
    c: Angle(g8,g9) = 1.5708
    c: Coincident(g10,g5)
    c: Coincident(g11,g6)
    c: Coincident(g11,g10)
    c: Coincident(g10,g9)
    c: Angle(g0,g11) = 2.00713
    c: Angle(g10,g1) = 1.8326
    c: PointOnObject(g0,g10)
    c: PointOnObject(g1,g10)
    c: Perpendicular(g11,g6)
    c: Coincident(g0,g-1)
    c: Distance(g0) = 450
    c: Distance(g9,g0) = 160
    c: Distance(g9) = 100
    c: DistanceY(g5,g6) = 950
    c: Equal(g6,g5)
    c: PointOnObject(g4,g0)
    c: PointOnObject(g1,g4)
    c: Coincident(g6,g12)
    c: Coincident(g12,g6)
    c: Coincident(g12,g13)
    c: Coincident(g13,g9)
    c: Coincident(g13,g14)
    c: Coincident(g14,g0)
    c: Coincident(g14,g15)
    c: Coincident(g15,g0)
    c: Coincident(g15,g16)
    c: Coincident(g16,g2)
    c: Coincident(g16,g17)
    c: Coincident(g17,g3)
    c: Coincident(g17,g18)
    c: Coincident(g18,g1)
    c: Coincident(g18,g19)
    c: Coincident(g19,g1)
    c: Coincident(g19,g20)
    c: Coincident(g20,g5)
    c: Coincident(g20,g21)
    c: Coincident(g21,g5)
    c: Coincident(g21,g22)
    c: Coincident(g22,g7)
    c: Coincident(g22,g23)
    c: Coincident(g23,g12)
    c: Coincident(g24,g19)
    c: Coincident(g24,g14)
    c: Coincident(g25,g4)
    c: Coincident(g25,g18)
    c: Coincident(g26,g22)
    c: Coincident(g26,g13)
    c: Coincident(g21,g27)
    c: Coincident(g27,g28)
    c: Coincident(g28,g20)
    c: Parallel(g26,g27)
    c: Parallel(g28,g20)
    c: Coincident(g29,g13)
    c: Coincident(g30,g15)
    c: Coincident(g30,g25)
    c: Coincident(g31,g13)
    c: Coincident(g31,g14)
    c: Coincident(g32,g33)
    c: Coincident(g33,g34)
    c: Coincident(g34,g35)
    c: Coincident(g35,g32)
    c: Perpendicular(g32,g35)
    c: Perpendicular(g33,g32)
    c: Perpendicular(g34,g33)
    c: Distance(g33) = 50
    c: Distance(g32) = 20
    c: Parallel(g35,g22)
    c: Distance(g34,g22) = 15
    c: DistanceY(g21,g34) = 120
    c: PointOnObject(g36,g13)
    c: Coincident(g36,g22)
    c: Perpendicular(g13,g36)
    c: Parallel(g14,g29)
    c: Coincident(g37,g29)
    c: PointOnObject(g37,g13)
    c: Perpendicular(g29,g37)
    c: Distance(g29) = 73
FEATURE [TechDraw::DrawSVGTemplate] Template002
  Height = 215.9
  Orientation = 1
  Template = <path>
  Width = 279.4
FEATURE [TechDraw::DrawProjGroupItem] ProjItem003  label="Side: cuts and assembly"
  CoarseView = false
  Direction = (0,1,0)
  Focus = 100
  HardHidden = false
  IsoCount = 0
  IsoHidden = false
  IsoVisible = false
  LockPosition = true
  Perspective = false
  Rotation = 0
  RotationVector = (1,0,0)
  Scale = 0.25
  ScaleType = 2
  ScrubCount = 0
  SeamHidden = false
  SeamVisible = false
  SmoothHidden = false
  SmoothVisible = true
  Source = -> [Sketch007]
  Type = 0
  X = 0
  XDirection = (-2e-16,0,1)
  Y = 0
FEATURE [TechDraw::DrawProjGroup] ProjGroup001
  Anchor = -> ProjItem003
  AutoDistribute = true
  LockPosition = false
  ProjectionType = 0
  Rotation = 0
  Scale = 0.25
  ScaleType = 2
  Source = -> [Sketch007]
  Views = -> [ProjItem003]
  X = 139.7
  Y = 107.95
  spacingX = 15
  spacingY = 15
FEATURE [TechDraw::DrawViewDimension] Dimension009
  AngleOverride = false
  Arbitrary = false
  ArbitraryTolerances = false
  EqualTolerance = true
  ExtensionAngle = 0
  FormatSpec = %.2w
  FormatSpecOverTolerance = %+.2w
  FormatSpecUnderTolerance = %+.2w
  Inverted = false
  LineAngle = 0
  LockPosition = false
  MeasureType = 1
  OverTolerance = 0
  References2D = -> [ProjItem003]
  Rotation = 0
  ScaleType = 0
  TheoreticalExact = false
  Type = 1
  UnderTolerance = 0
  X = -57.6035
  Y = 87.4336
FEATURE [TechDraw::DrawViewDimension] Dimension010
  AngleOverride = false
  Arbitrary = false
  ArbitraryTolerances = false
  EqualTolerance = true
  ExtensionAngle = 0
  FormatSpec = %.0w
  FormatSpecOverTolerance = %+.2w
  FormatSpecUnderTolerance = %+.2w
  Inverted = false
  LineAngle = 0
  LockPosition = false
  MeasureType = 1
  OverTolerance = 0
  References2D = -> [ProjItem003]
  Rotation = 0
  ScaleType = 0
  TheoreticalExact = false
  Type = 0
  UnderTolerance = 0
  X = 9.17622
  Y = 69.367
FEATURE [TechDraw::DrawViewDimension] Dimension011
  AngleOverride = false
  Arbitrary = false
  ArbitraryTolerances = false
  EqualTolerance = true
  ExtensionAngle = 0
  FormatSpec = %.2w
  FormatSpecOverTolerance = %+.2w
  FormatSpecUnderTolerance = %+.2w
  Inverted = false
  LineAngle = 0
  LockPosition = false
  MeasureType = 1
  OverTolerance = 0
  References2D = -> [ProjItem003]
  Rotation = 0
  ScaleType = 0
  TheoreticalExact = false
  Type = 6
  UnderTolerance = 0
  X = -110.966
  Y = 74.4624
FEATURE [TechDraw::DrawViewDimension] Dimension012
  AngleOverride = false
  Arbitrary = false
  ArbitraryTolerances = false
  EqualTolerance = true
  ExtensionAngle = 0
  FormatSpec = %.2w
  FormatSpecOverTolerance = %+.2w
  FormatSpecUnderTolerance = %+.2w
  Inverted = false
  LineAngle = 0
  LockPosition = false
  MeasureType = 1
  OverTolerance = 0
  References2D = -> [ProjItem003]
  Rotation = 0
  ScaleType = 0
  TheoreticalExact = false
  Type = 6
  UnderTolerance = 0
  X = -5.30021
  Y = 66.6813
FEATURE [TechDraw::DrawViewDimension] Dimension013
  AngleOverride = false
  Arbitrary = false
  ArbitraryTolerances = false
  EqualTolerance = true
  ExtensionAngle = 0
  FormatSpec = %.2w
  FormatSpecOverTolerance = %+.2w
  FormatSpecUnderTolerance = %+.2w
  Inverted = false
  LineAngle = 0
  LockPosition = false
  MeasureType = 1
  OverTolerance = 0
  References2D = -> [ProjItem003]
  Rotation = 0
  ScaleType = 0
  TheoreticalExact = false
  Type = 0
  UnderTolerance = 0
  X = -9.57407
  Y = 44.5071
FEATURE [TechDraw::DrawViewDimension] Dimension014
  AngleOverride = false
  Arbitrary = false
  ArbitraryTolerances = false
  EqualTolerance = true
  ExtensionAngle = 0
  FormatSpec = %.0w
  FormatSpecOverTolerance = %+.2w
  FormatSpecUnderTolerance = %+.2w
  Inverted = false
  LineAngle = 0
  LockPosition = false
  MeasureType = 1
  OverTolerance = 0
  References2D = -> [ProjItem003]
  Rotation = 0
  ScaleType = 0
  TheoreticalExact = false
  Type = 0
  UnderTolerance = 0
  X = -23.5859
  Y = 10.523
FEATURE [TechDraw::DrawViewDimension] Dimension015
  AngleOverride = false
  Arbitrary = false
  ArbitraryTolerances = false
  EqualTolerance = true
  ExtensionAngle = 0
  FormatSpec = %.2w
  FormatSpecOverTolerance = %+.2w
  FormatSpecUnderTolerance = %+.2w
  Inverted = false
  LineAngle = 0
  LockPosition = false
  MeasureType = 1
  OverTolerance = 0
  References2D = -> [ProjItem003]
  Rotation = 0
  ScaleType = 0
  TheoreticalExact = false
  Type = 0
  UnderTolerance = 0
  X = 42.6549
  Y = -35.5068
FEATURE [TechDraw::DrawViewDimension] Dimension016
  AngleOverride = false
  Arbitrary = false
  ArbitraryTolerances = false
  EqualTolerance = true
  ExtensionAngle = 0
  FormatSpec = %.0w
  FormatSpecOverTolerance = %+.2w
  FormatSpecUnderTolerance = %+.2w
  Inverted = false
  LineAngle = 0
  LockPosition = false
  MeasureType = 1
  OverTolerance = 0
  References2D = -> [ProjItem003]
  Rotation = 0
  ScaleType = 0
  TheoreticalExact = false
  Type = 0
  UnderTolerance = 0
  X = -34.5701
  Y = -64.0785
FEATURE [TechDraw::DrawViewDimension] Dimension017
  AngleOverride = false
  Arbitrary = false
  ArbitraryTolerances = false
  EqualTolerance = true
  ExtensionAngle = 0
  FormatSpec = %.0w
  FormatSpecOverTolerance = %+.2w
  FormatSpecUnderTolerance = %+.2w
  Inverted = false
  LineAngle = 0
  LockPosition = false
  MeasureType = 1
  OverTolerance = 0
  References2D = -> [ProjItem003]
  Rotation = 0
  ScaleType = 0
  TheoreticalExact = false
  Type = 6
  UnderTolerance = 0
  X = 35.4062
  Y = -28.042
FEATURE [TechDraw::DrawViewDimension] Dimension018
  AngleOverride = false
  Arbitrary = false
  ArbitraryTolerances = false
  EqualTolerance = true
  ExtensionAngle = 0
  FormatSpec = %.0w
  FormatSpecOverTolerance = %+.2w
  FormatSpecUnderTolerance = %+.2w
  Inverted = false
  LineAngle = 0
  LockPosition = false
  MeasureType = 1
  OverTolerance = 0
  References2D = -> [ProjItem003]
  Rotation = 0
  ScaleType = 0
  TheoreticalExact = false
  Type = 6
  UnderTolerance = 0
  X = 52.3581
  Y = -44.7756
FEATURE [TechDraw::DrawViewDimension] Dimension019
  AngleOverride = false
  Arbitrary = false
  ArbitraryTolerances = false
  EqualTolerance = true
  ExtensionAngle = 0
  FormatSpec = %.2w
  FormatSpecOverTolerance = %+.2w
  FormatSpecUnderTolerance = %+.2w
  Inverted = false
  LineAngle = 0
  LockPosition = false
  MeasureType = 1
  OverTolerance = 0
  References2D = -> [ProjItem003]
  Rotation = 0
  ScaleType = 0
  TheoreticalExact = false
  Type = 6
  UnderTolerance = 0
  X = 115.845
  Y = -60.2395
FEATURE [TechDraw::DrawViewDimension] Dimension020
  AngleOverride = false
  Arbitrary = false
  ArbitraryTolerances = false
  EqualTolerance = true
  ExtensionAngle = 0
  FormatSpec = %.0w
  FormatSpecOverTolerance = %+.2w
  FormatSpecUnderTolerance = %+.2w
  Inverted = false
  LineAngle = 0
  LockPosition = false
  MeasureType = 1
  OverTolerance = 0
  References2D = -> [ProjItem003]
  Rotation = 0
  ScaleType = 0
  TheoreticalExact = false
  Type = 6
  UnderTolerance = 0
  X = -111.366
  Y = -68.2068
FEATURE [TechDraw::DrawViewDimension] Dimension021
  AngleOverride = false
  Arbitrary = false
  ArbitraryTolerances = false
  EqualTolerance = true
  ExtensionAngle = 0
  FormatSpec = %.2w
  FormatSpecOverTolerance = %+.2w
  FormatSpecUnderTolerance = %+.2w
  Inverted = false
  LineAngle = 0
  LockPosition = false
  MeasureType = 1
  OverTolerance = 0
  References2D = -> [ProjItem003]
  Rotation = 0
  ScaleType = 0
  TheoreticalExact = false
  Type = 6
  UnderTolerance = 0
  X = -15.2572
  Y = -31.7657
FEATURE [TechDraw::DrawViewDimension] Dimension022
  AngleOverride = false
  Arbitrary = false
  ArbitraryTolerances = false
  EqualTolerance = true
  ExtensionAngle = 0
  FormatSpec = %.2w
  FormatSpecOverTolerance = %+.2w
  FormatSpecUnderTolerance = %+.2w
  Inverted = false
  LineAngle = 0
  LockPosition = false
  MeasureType = 1
  OverTolerance = 0
  References2D = -> [ProjItem003]
  Rotation = 0
  ScaleType = 0
  TheoreticalExact = false
  Type = 6
  UnderTolerance = 0
  X = -14.4235
  Y = 54.6918
FEATURE [TechDraw::DrawViewDimension] Dimension023
  AngleOverride = false
  Arbitrary = false
  ArbitraryTolerances = false
  EqualTolerance = true
  ExtensionAngle = 0
  FormatSpec = %.0w
  FormatSpecOverTolerance = %+.2w
  FormatSpecUnderTolerance = %+.2w
  Inverted = false
  LineAngle = 0
  LockPosition = false
  MeasureType = 1
  OverTolerance = 0
  References2D = -> [ProjItem003]
  Rotation = 0
  ScaleType = 0
  TheoreticalExact = false
  Type = 0
  UnderTolerance = 0
  X = 80.6475
  Y = -34.2318
FEATURE [TechDraw::DrawViewDimension] Dimension024
  AngleOverride = false
  Arbitrary = false
  ArbitraryTolerances = false
  EqualTolerance = true
  ExtensionAngle = 0
  FormatSpec = %.0w
  FormatSpecOverTolerance = %+.2w
  FormatSpecUnderTolerance = %+.2w
  Inverted = false
  LineAngle = 0
  LockPosition = false
  MeasureType = 1
  OverTolerance = 0
  References2D = -> [ProjItem003]
  Rotation = 0
  ScaleType = 0
  TheoreticalExact = false
  Type = 6
  UnderTolerance = 0
  X = 47.0265
  Y = -29.5897
FEATURE [TechDraw::DrawViewDimension] Dimension025
  AngleOverride = false
  Arbitrary = false
  ArbitraryTolerances = false
  EqualTolerance = true
  ExtensionAngle = 0
  FormatSpec = %.0w
  FormatSpecOverTolerance = %+.2w
  FormatSpecUnderTolerance = %+.2w
  Inverted = false
  LineAngle = 0
  LockPosition = false
  MeasureType = 1
  OverTolerance = 0
  References2D = -> [ProjItem003]
  Rotation = 0
  ScaleType = 0
  TheoreticalExact = false
  Type = 0
  UnderTolerance = 0
  X = 78.9976
  Y = -59.0075
FEATURE [TechDraw::DrawViewDimension] Dimension026
  AngleOverride = false
  Arbitrary = false
  ArbitraryTolerances = false
  EqualTolerance = true
  ExtensionAngle = 0
  FormatSpec = %.2w
  FormatSpecOverTolerance = %+.2w
  FormatSpecUnderTolerance = %+.2w
  Inverted = false
  LineAngle = 0
  LockPosition = false
  MeasureType = 1
  OverTolerance = 0
  References2D = -> [ProjItem003]
  Rotation = 0
  ScaleType = 0
  TheoreticalExact = false
  Type = 0
  UnderTolerance = 0
  X = 119.81
  Y = -65.1059
FEATURE [TechDraw::DrawViewDimension] Dimension027
  AngleOverride = false
  Arbitrary = false
  ArbitraryTolerances = false
  EqualTolerance = true
  ExtensionAngle = 0
  FormatSpec = %.0w
  FormatSpecOverTolerance = %+.2w
  FormatSpecUnderTolerance = %+.2w
  Inverted = false
  LineAngle = 0
  LockPosition = false
  MeasureType = 1
  OverTolerance = 0
  References2D = -> [ProjItem003]
  Rotation = 0
  ScaleType = 0
  TheoreticalExact = false
  Type = 0
  UnderTolerance = 0
  X = -121.756
  Y = -70.7358
FEATURE [TechDraw::DrawViewDimension] Dimension028
  AngleOverride = false
  Arbitrary = false
  ArbitraryTolerances = false
  EqualTolerance = true
  ExtensionAngle = 0
  FormatSpec = %.2w
  FormatSpecOverTolerance = %+.2w
  FormatSpecUnderTolerance = %+.2w
  Inverted = false
  LineAngle = 0
  LockPosition = false
  MeasureType = 1
  OverTolerance = 0
  References2D = -> [ProjItem002]
  Rotation = 0
  ScaleType = 0
  TheoreticalExact = false
  Type = 0
  UnderTolerance = 0
  X = 12.9492
  Y = -1.51352
FEATURE [TechDraw::DrawViewDimension] Dimension029
  AngleOverride = false
  Arbitrary = false
  ArbitraryTolerances = false
  EqualTolerance = true
  ExtensionAngle = 0
  FormatSpec = %.2w
  FormatSpecOverTolerance = %+.2w
  FormatSpecUnderTolerance = %+.2w
  Inverted = false
  LineAngle = 0
  LockPosition = false
  MeasureType = 1
  OverTolerance = 0
  References2D = -> [ProjItem002]
  Rotation = 0
  ScaleType = 0
  TheoreticalExact = false
  Type = 2
  UnderTolerance = 0
  X = 3.25079
  Y = 3.90041
FEATURE [TechDraw::DrawViewDimension] Dimension030
  AngleOverride = false
  Arbitrary = false
  ArbitraryTolerances = false
  EqualTolerance = true
  ExtensionAngle = 0
  FormatSpec = %.2w
  FormatSpecOverTolerance = %+.2w
  FormatSpecUnderTolerance = %+.2w
  Inverted = false
  LineAngle = 0
  LockPosition = false
  MeasureType = 1
  OverTolerance = 0
  References2D = -> [ProjItem002]
  Rotation = 0
  ScaleType = 0
  TheoreticalExact = false
  Type = 0
  UnderTolerance = 0
  X = 10.9156
  Y = 5.86312
FEATURE [TechDraw::DrawViewDimension] Dimension031
  AngleOverride = false
  Arbitrary = false
  ArbitraryTolerances = false
  EqualTolerance = true
  ExtensionAngle = 0
  FormatSpec = %.2w
  FormatSpecOverTolerance = %+.2w
  FormatSpecUnderTolerance = %+.2w
  Inverted = false
  LineAngle = 0
  LockPosition = false
  MeasureType = 1
  OverTolerance = 0
  References2D = -> [ProjItem002]
  Rotation = 0
  ScaleType = 0
  TheoreticalExact = false
  Type = 0
  UnderTolerance = 0
  X = -11.5844
  Y = -0.856552
FEATURE [TechDraw::DrawViewDimension] Dimension032
  AngleOverride = false
  Arbitrary = false
  ArbitraryTolerances = false
  EqualTolerance = true
  ExtensionAngle = 0
  FormatSpec = %.2w
  FormatSpecOverTolerance = %+.2w
  FormatSpecUnderTolerance = %+.2w
  Inverted = false
  LineAngle = 0
  LockPosition = false
  MeasureType = 1
  OverTolerance = 0
  References2D = -> [ProjItem002]
  Rotation = 0
  ScaleType = 0
  TheoreticalExact = false
  Type = 0
  UnderTolerance = 0
  X = 0.613117
  Y = -0.854124
FEATURE [TechDraw::DrawPage] Page001  label="SlatDraw"
  KeepUpdated = true
  NextBalloonIndex = 1
  ProjectionType = 0
  Template = -> Template001
  Views = -> [ProjGroup,Dimension001,Dimension003,Dimension004,Dimension005,Dimension006,Dimension007,Dimension008,Dimension028,Dimension029,Dimension030,Dimension031,Dimension032]
FEATURE [TechDraw::DrawViewDimension] Dimension033
  AngleOverride = false
  Arbitrary = false
  ArbitraryTolerances = false
  EqualTolerance = true
  ExtensionAngle = 0
  FormatSpec = %.0w
  FormatSpecOverTolerance = %+.2w
  FormatSpecUnderTolerance = %+.2w
  Inverted = false
  LineAngle = 0
  LockPosition = false
  MeasureType = 1
  OverTolerance = 0
  References2D = -> [ProjItem003]
  Rotation = 0
  ScaleType = 0
  TheoreticalExact = false
  Type = 0
  UnderTolerance = 0
  X = 15.1829
  Y = -23.5686
FEATURE [TechDraw::DrawViewBalloon] Balloon
  BubbleShape = 3
  EndType = 0
  EndTypeScale = 1
  KinkLength = 5
  LockPosition = false
  OriginX = 239.308
  OriginY = -85.6112
  Rotation = 0
  ScaleType = 0
  ShapeScale = 1
  SourceView = -> ProjItem003
  Text = Dashed lines: area left for clamping
  TextWrapLen = -1
  X = 319.308
  Y = -5.6112
FEATURE [TechDraw::DrawViewDimension] Dimension034
  AngleOverride = false
  Arbitrary = false
  ArbitraryTolerances = false
  EqualTolerance = true
  ExtensionAngle = 0
  FormatSpec = %.2w
  FormatSpecOverTolerance = %+.2w
  FormatSpecUnderTolerance = %+.2w
  Inverted = false
  LineAngle = 0
  LockPosition = false
  MeasureType = 1
  OverTolerance = 0
  References2D = -> [ProjItem003]
  Rotation = 0
  ScaleType = 0
  TheoreticalExact = false
  Type = 0
  UnderTolerance = 0
  X = -81.9035
  Y = -67.5143
FEATURE [TechDraw::DrawViewDimension] Dimension035
  AngleOverride = false
  Arbitrary = false
  ArbitraryTolerances = false
  EqualTolerance = true
  ExtensionAngle = 0
  FormatSpec = %.2w
  FormatSpecOverTolerance = %+.2w
  FormatSpecUnderTolerance = %+.2w
  Inverted = false
  LineAngle = 0
  LockPosition = false
  MeasureType = 1
  OverTolerance = 0
  References2D = -> [ProjItem003]
  Rotation = 0
  ScaleType = 0
  TheoreticalExact = false
  Type = 0
  UnderTolerance = 0
  X = -89.4309
  Y = -64.7156
FEATURE [TechDraw::DrawViewBalloon] Balloon001
  BubbleShape = 3
  EndType = 0
  EndTypeScale = 1
  KinkLength = 5
  LockPosition = false
  OriginX = -335.414
  OriginY = -258.29
  Rotation = 0
  ScaleType = 0
  ShapeScale = 1
  SourceView = -> ProjItem003
  Text = Stretcher position
  TextWrapLen = -1
  X = -225.559
  Y = -158.972
FEATURE [TechDraw::DrawViewDimension] Dimension036
  AngleOverride = false
  Arbitrary = false
  ArbitraryTolerances = false
  EqualTolerance = true
  ExtensionAngle = 0
  FormatSpec = %.2w
  FormatSpecOverTolerance = %+.2w
  FormatSpecUnderTolerance = %+.2w
  Inverted = false
  LineAngle = 0
  LockPosition = false
  MeasureType = 1
  OverTolerance = 0
  References2D = -> [ProjItem003]
  Rotation = 0
  ScaleType = 0
  TheoreticalExact = false
  Type = 0
  UnderTolerance = 0
  X = -69.6577
  Y = -65.0956
FEATURE [TechDraw::DrawViewDimension] Dimension037
  AngleOverride = false
  Arbitrary = false
  ArbitraryTolerances = false
  EqualTolerance = true
  ExtensionAngle = 0
  FormatSpec = %.0w
  FormatSpecOverTolerance = %+.2w
  FormatSpecUnderTolerance = %+.2w
  Inverted = false
  LineAngle = 0
  LockPosition = false
  MeasureType = 1
  OverTolerance = 0
  References2D = -> [ProjItem003]
  Rotation = 0
  ScaleType = 0
  TheoreticalExact = false
  Type = 0
  UnderTolerance = 0
  X = -102.646
  Y = -74.6329
FEATURE [TechDraw::DrawViewDimension] Dimension038
  AngleOverride = false
  Arbitrary = false
  ArbitraryTolerances = false
  EqualTolerance = true
  ExtensionAngle = 0
  FormatSpec = %.2w
  FormatSpecOverTolerance = %+.2w
  FormatSpecUnderTolerance = %+.2w
  Inverted = false
  LineAngle = 0
  LockPosition = false
  MeasureType = 1
  OverTolerance = 0
  References2D = -> [View002]
  Rotation = 0
  ScaleType = 0
  TheoreticalExact = false
  Type = 0
  UnderTolerance = 0
  X = -54.9068
  Y = 183.126
FEATURE [TechDraw::DrawPage] Page  label="SideDrillTemplate"
  KeepUpdated = true
  NextBalloonIndex = 1
  ProjectionType = 0
  Template = -> Template
  Views = -> [View002,Dimension,Dimension038]
FEATURE [App::Part] Part  label="TheChair"
  Origin = -> Origin003
FEATURE [PartDesign::Boolean] Boolean
  Group = -> [Body,Clone,Body002,PathArray,PathArray001]
  Type = 0
FEATURE [PartDesign::Body] Body003  label="FusedChair"
  Group = -> [Boolean]
  Origin = -> Origin004
  Tip = -> Boolean
FEATURE [TechDraw::DrawViewDimension] Dimension039
  AngleOverride = false
  Arbitrary = false
  ArbitraryTolerances = false
  EqualTolerance = true
  ExtensionAngle = 0
  FormatSpec = %.0w
  FormatSpecOverTolerance = %+.2w
  FormatSpecUnderTolerance = %+.2w
  Inverted = false
  LineAngle = 0
  LockPosition = false
  MeasureType = 1
  OverTolerance = 0
  References2D = -> [ProjItem003]
  Rotation = 0
  ScaleType = 0
  TheoreticalExact = false
  Type = 0
  UnderTolerance = 0
  X = 49.2696
  Y = -37.4246
FEATURE [TechDraw::DrawPage] Page002  label="Cuts"
  KeepUpdated = true
  NextBalloonIndex = 3
  ProjectionType = 0
  Template = -> Template002
  Views = -> [ProjGroup001,Dimension009,Dimension010,Dimension011,Dimension012,Dimension013,Dimension014,Dimension015,Dimension016,Dimension017,Dimension018,Dimension019,Dimension020,Dimension021,Dimension022,Dimension023,Dimension024,Dimension025,Dimension026,Dimension027,Dimension033,Balloon,Dimension034,Dimension035,Balloon001,Dimension036,Dimension037,Dimension039]
note: 3 file-system paths scrubbed to <path> (originals preserved in the JSON sidecar)
